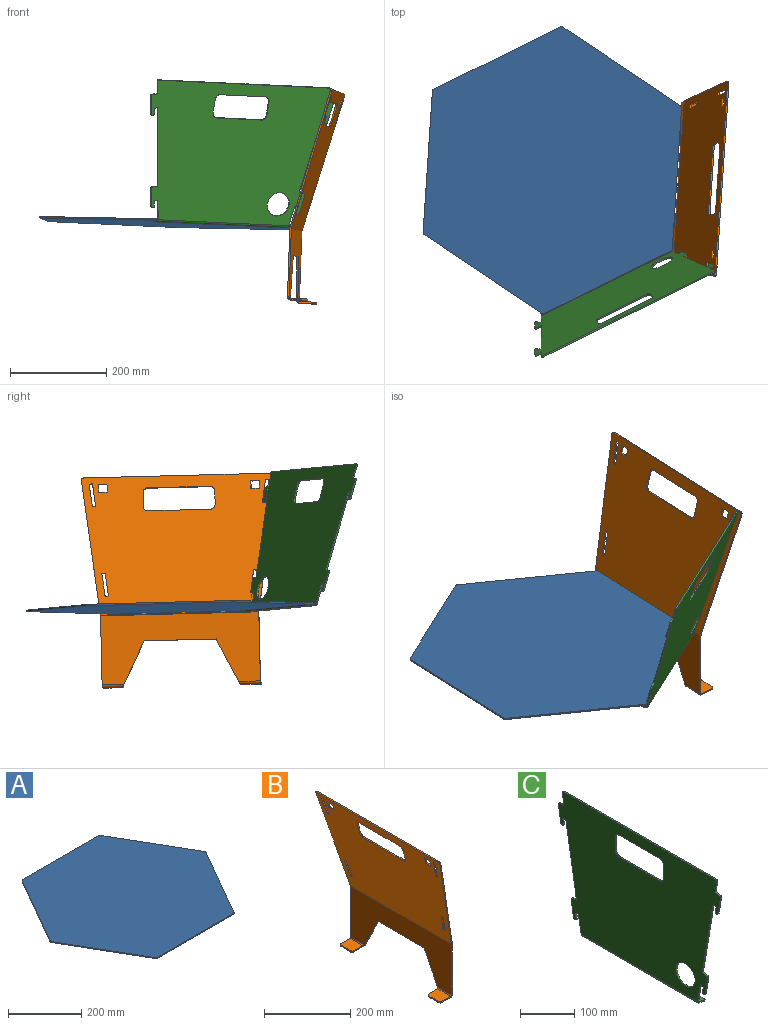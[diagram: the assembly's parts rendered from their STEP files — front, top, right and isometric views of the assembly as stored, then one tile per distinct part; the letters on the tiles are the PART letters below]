
ASSEMBLY  parts=3 mates=3
PART A: 14 faces, bbox 598.5x519.6x3 mm
  f0: plane 294.23x3mm, normal (0,-1,0), area 882.7mm2, adj f6,f7,f8,f13
  f1: plane 254.81x147.11mm, normal (0.87,-0.5,0), area 882.7mm2, adj f6,f7,f8,f9
  f2: plane 254.81x147.11mm, normal (0.87,0.5,0), area 882.7mm2, adj f6,f7,f9,f10
  f3: plane 294.23x3mm, normal (0,1,0), area 882.7mm2, adj f6,f7,f10,f11
  f4: plane 254.81x147.11mm, normal (-0.87,0.5,0), area 882.7mm2, adj f6,f7,f11,f12
  f5: plane 254.81x147.11mm, normal (-0.87,-0.5,0), area 882.7mm2, adj f6,f7,f12,f13
  f6: plane 598.45x519.62mm, normal (0,0,1), area 233818.8mm2, adj f0,f1,f2,f3,f4,f5,f8,f9
  f7: plane 598.45x519.62mm, normal (0,0,-1), area 233818.8mm2, adj f0,f1,f2,f3,f4,f5,f8,f9
  f8: cylinder r=5mm len=4.33mm, axis (0,0,-1), area 15.7mm2, adj f0,f1,f6,f7
  f9: cylinder r=5mm len=5mm, axis (0,0,-1), area 15.7mm2, adj f1,f2,f6,f7
  f10: cylinder r=5mm len=4.33mm, axis (0,0,-1), area 15.7mm2, adj f2,f3,f6,f7
  f11: cylinder r=5mm len=4.33mm, axis (0,0,-1), area 15.7mm2, adj f3,f4,f6,f7
  f12: cylinder r=5mm len=5mm, axis (0,0,-1), area 15.7mm2, adj f4,f5,f6,f7
  f13: cylinder r=5mm len=4.33mm, axis (0,0,-1), area 15.7mm2, adj f0,f5,f6,f7
PART B: 72 faces, bbox 80.7x407x439.8 mm
  f0: plane 150x3.18mm, normal (0,0,-1), area 476.3mm2, adj f1,f4,f5,f6
  f1: plane 89.53x44.76mm, normal (0,0.89,-0.45), area 317.8mm2, adj f0,f5,f6,f58
  f2: plane 143.8x3.18mm, normal (0,-1,0), area 456.6mm2, adj f5,f6,f46,f57
  f3: plane 143.8x3.18mm, normal (0,1,0), area 456.6mm2, adj f5,f6,f47,f69
  f4: plane 89.53x44.76mm, normal (0,-0.89,-0.45), area 317.8mm2, adj f0,f5,f6,f68
  f5: plane 330x143.8mm, normal (-1,0,0), area 30019.3mm2, adj f0,f1,f2,f3,f4,f49,f60,f71
  f6: plane 330x143.8mm, normal (1,0,0), area 30019.3mm2, adj f0,f1,f2,f3,f4,f48,f59,f70
  f7: plane 407.03x289.08mm, normal (0.97,0,0.26), area 101115mm2, adj f8,f10,f11,f12,f13,f14,f15,f16
  f8: plane 284.45x79.06mm, normal (0.03,-0.99,-0.13), area 940.2mm2, adj f7,f9,f45,f46
  f9: plane 407.03x289.08mm, normal (-0.97,0,-0.26), area 101115mm2, adj f8,f10,f11,f12,f13,f14,f15,f16
  f10: plane 284.45x79.06mm, normal (0.03,0.99,-0.13), area 940.2mm2, adj f7,f9,f44,f47
  f11: plane 130x3.07mm, normal (0.26,0,-0.97), area 412.7mm2, adj f7,f9,f12,f43
  f12: cylinder r=10mm len=10.48mm, axis (-0.97,0,-0.26), area 49.9mm2, adj f7,f9,f11,f13
  f13: plane 29.8x10.83mm, normal (0,1,0), area 95.2mm2, adj f7,f9,f12,f14
  f14: cylinder r=10mm len=10.48mm, axis (-0.97,0,-0.26), area 49.9mm2, adj f7,f9,f13,f15
  f15: plane 130x3.07mm, normal (-0.26,0,0.97), area 412.8mm2, adj f7,f9,f14,f16
  f16: cylinder r=10mm len=10.48mm, axis (-0.97,0,-0.26), area 49.9mm2, adj f7,f9,f15,f17
  f17: plane 29.8x10.83mm, normal (0,-1,0), area 95.3mm2, adj f7,f9,f16,f43
  f18: plane 48.71x15.9mm, normal (0.03,-0.99,-0.13), area 158.8mm2, adj f7,f9,f19,f42
  f19: plane 6.94x3.3mm, normal (0.26,0.13,-0.96), area 22.2mm2, adj f7,f9,f18,f20
  f20: plane 48.71x15.9mm, normal (-0.03,0.99,0.13), area 158.8mm2, adj f7,f9,f19,f42
  f21: plane 17.24x7.47mm, normal (0,-1,0), area 54mm2, adj f7,f9,f22,f41
  f22: plane 17x3.07mm, normal (0.26,0,-0.97), area 54mm2, adj f7,f9,f21,f23
  f23: plane 17.24x7.47mm, normal (0,1,0), area 54mm2, adj f7,f9,f22,f41
  f24: plane 48.71x15.9mm, normal (0.03,-0.99,-0.13), area 158.8mm2, adj f7,f9,f25,f40
  f25: plane 6.94x3.3mm, normal (0.26,0.13,-0.96), area 22.2mm2, adj f7,f9,f24,f26
  f26: plane 48.71x15.9mm, normal (-0.03,0.99,0.13), area 158.7mm2, adj f7,f9,f25,f40
  f27: plane 17.24x7.47mm, normal (0,-1,0), area 54mm2, adj f7,f9,f28,f39
  f28: plane 17x3.07mm, normal (0.26,0,-0.97), area 54mm2, adj f7,f9,f27,f29
  f29: plane 17.24x7.47mm, normal (0,1,0), area 54mm2, adj f7,f9,f28,f39
  f30: plane 6.94x3.3mm, normal (0.26,-0.13,-0.96), area 22.2mm2, adj f7,f9,f31,f38
  f31: plane 48.71x15.9mm, normal (0.03,0.99,-0.13), area 158.8mm2, adj f7,f9,f30,f32
  f32: plane 6.94x3.3mm, normal (-0.26,0.13,0.96), area 22.2mm2, adj f7,f9,f31,f38
  f33: plane 6.94x3.3mm, normal (0.26,-0.13,-0.96), area 22.2mm2, adj f7,f9,f34,f37
  f34: plane 48.71x15.9mm, normal (0.03,0.99,-0.13), area 158.7mm2, adj f7,f9,f33,f35
  f35: plane 6.94x3.3mm, normal (-0.26,0.13,0.96), area 22.2mm2, adj f7,f9,f34,f37
  f36: plane 397.03x3.07mm, normal (-0.26,0,0.97), area 1260.6mm2, adj f7,f9,f44,f45
  f37: plane 48.71x15.9mm, normal (-0.03,-0.99,0.13), area 158.7mm2, adj f7,f9,f33,f35
  f38: plane 48.71x15.9mm, normal (-0.03,-0.99,0.13), area 158.7mm2, adj f7,f9,f30,f32
  f39: plane 17x3.07mm, normal (-0.26,0,0.97), area 54mm2, adj f7,f9,f27,f29
  f40: plane 6.94x3.3mm, normal (-0.26,-0.13,0.96), area 22.2mm2, adj f7,f9,f24,f26
  f41: plane 17x3.07mm, normal (-0.26,0,0.97), area 54mm2, adj f7,f9,f21,f23
  f42: plane 6.94x3.3mm, normal (-0.26,-0.13,0.96), area 22.2mm2, adj f7,f9,f18,f20
  f43: cylinder r=10mm len=10.48mm, axis (-0.97,0,-0.26), area 49.9mm2, adj f7,f9,f11,f17
  f44: cylinder r=5mm len=6.28mm, axis (0.97,0,0.26), area 27mm2, adj f7,f9,f10,f36
  f45: cylinder r=5mm len=6.28mm, axis (0.97,0,0.26), area 27mm2, adj f7,f8,f9,f36
  f46: bspline ~3.25x1.42mm, area 3.2mm2, adj f2,f8,f48,f49
  f47: bspline ~3.25x1.42mm, area 3.2mm2, adj f3,f10,f48,f49
  f48: cylinder r=5.47mm len=330.16mm, axis (0,-1,0), area 473.1mm2, adj f6,f7,f46,f47
  f49: cylinder r=2.3mm len=330.16mm, axis (0,-1,0), area 198.8mm2, adj f5,f9,f46,f47
  f50: plane 32.5x3.18mm, normal (-1,0,0), area 103.2mm2, adj f53,f54,f55,f56
  f51: plane 29.53x3.18mm, normal (0,-1,0), area 93.7mm2, adj f53,f54,f55,f57
  f52: plane 29.53x3.18mm, normal (0,1,0), area 93.7mm2, adj f53,f54,f56,f58
  f53: plane 42.5x34.53mm, normal (0,0,1), area 1456.6mm2, adj f50,f51,f52,f55,f56,f60
  f54: plane 42.5x34.53mm, normal (0,0,-1), area 1456.6mm2, adj f50,f51,f52,f55,f56,f59
  f55: cylinder r=5mm len=5mm, axis (0,0,1), area 24.9mm2, adj f50,f51,f53,f54
  f56: cylinder r=5mm len=5mm, axis (0,0,1), area 24.9mm2, adj f50,f52,f53,f54
  f57: plane 5.48x5.48mm, normal (0,-1,0), area 19.4mm2, adj f2,f51,f59,f60
  f58: bspline ~5.48x5.48mm, area 21.7mm2, adj f1,f52,f59,f60
  f59: cylinder r=5.47mm len=45.24mm, axis (0,-1,0), area 374mm2, adj f6,f54,f57,f58
  f60: cylinder r=2.3mm len=45.24mm, axis (0,-1,0), area 157.1mm2, adj f5,f53,f57,f58
  f61: plane 29.53x3.18mm, normal (0,1,0), area 93.7mm2, adj f64,f65,f67,f69
  f62: plane 32.5x3.18mm, normal (-1,0,0), area 103.2mm2, adj f64,f65,f66,f67
  f63: plane 29.53x3.18mm, normal (0,-1,0), area 93.7mm2, adj f64,f65,f66,f68
  f64: plane 42.5x34.53mm, normal (0,0,1), area 1456.6mm2, adj f61,f62,f63,f66,f67,f71
  f65: plane 42.5x34.53mm, normal (0,0,-1), area 1456.6mm2, adj f61,f62,f63,f66,f67,f70
  f66: cylinder r=5mm len=5mm, axis (0,0,1), area 24.9mm2, adj f62,f63,f64,f65
  f67: cylinder r=5mm len=5mm, axis (0,0,1), area 24.9mm2, adj f61,f62,f64,f65
  f68: bspline ~5.48x5.48mm, area 21.7mm2, adj f4,f63,f70,f71
  f69: plane 5.48x5.48mm, normal (0,1,0), area 19.4mm2, adj f3,f61,f70,f71
  f70: cylinder r=5.47mm len=45.24mm, axis (0,-1,0), area 374.1mm2, adj f6,f65,f68,f69
  f71: cylinder r=2.3mm len=45.24mm, axis (0,-1,0), area 157.1mm2, adj f5,f64,f68,f69
PART C: 63 faces, bbox 22.5x422.1x308.2 mm
  f0: plane 30x3.18mm, normal (0,-1,0), area 95.2mm2, adj f1,f35,f36,f37
  f1: cylinder r=10mm len=10mm, axis (-1,0,0), area 49.9mm2, adj f0,f2,f36,f37
  f2: plane 105x3.18mm, normal (0,0,-1), area 333.4mm2, adj f1,f3,f36,f37
  f3: cylinder r=10mm len=10mm, axis (-1,0,0), area 49.9mm2, adj f2,f4,f36,f37
  f4: plane 30x3.18mm, normal (0,1,0), area 95.2mm2, adj f3,f5,f36,f37
  f5: cylinder r=10mm len=10mm, axis (-1,0,0), area 49.9mm2, adj f4,f6,f36,f37
  f6: plane 105x3.18mm, normal (0,0,1), area 333.4mm2, adj f5,f35,f36,f37
  f7: plane 11.84x3.18mm, normal (0,0.17,0.99), area 38.1mm2, adj f34,f36,f37,f50
  f8: plane 38.46x6.45mm, normal (0,0.99,-0.17), area 123.8mm2, adj f36,f37,f43,f50
  f9: plane 3.18x0.99mm, normal (0,-0.17,-0.99), area 3.2mm2, adj f36,f37,f40,f43
  f10: plane 11.84x3.18mm, normal (0,-0.99,0.17), area 38.1mm2, adj f11,f36,f37,f40
  f11: plane 7.89x3.18mm, normal (0,-0.17,-0.99), area 25.4mm2, adj f10,f12,f36,f37
  f12: plane 167.66x28.1mm, normal (0,0.99,-0.17), area 539.8mm2, adj f11,f13,f36,f37
  f13: plane 11.84x3.18mm, normal (0,0.17,0.99), area 38.1mm2, adj f12,f36,f37,f51
  f14: plane 38.46x6.45mm, normal (0,0.99,-0.17), area 123.8mm2, adj f36,f37,f49,f51
  f15: plane 3.18x0.99mm, normal (0,-0.17,-0.99), area 3.2mm2, adj f36,f37,f48,f49
  f16: plane 11.84x3.18mm, normal (0,-0.99,0.17), area 38.1mm2, adj f17,f36,f37,f48
  f17: plane 7.89x3.18mm, normal (0,-0.17,-0.99), area 25.4mm2, adj f16,f18,f36,f37
  f18: plane 41.88x7.02mm, normal (0,0.99,-0.17), area 134.8mm2, adj f17,f36,f37,f60
  f19: plane 41.88x7.02mm, normal (0,-0.99,-0.17), area 134.8mm2, adj f20,f36,f37,f59
  f20: plane 7.89x3.18mm, normal (0,0.17,-0.99), area 25.4mm2, adj f19,f21,f36,f37
  f21: plane 11.84x3.18mm, normal (0,0.99,0.17), area 38.1mm2, adj f20,f36,f37,f38
  f22: plane 3.18x0.99mm, normal (0,0.17,-0.99), area 3.2mm2, adj f36,f37,f38,f41
  f23: plane 38.46x6.45mm, normal (0,-0.99,-0.17), area 123.8mm2, adj f36,f37,f41,f46
  f24: plane 11.84x3.18mm, normal (0,-0.17,0.99), area 38.1mm2, adj f25,f36,f37,f46
  f25: plane 167.66x28.1mm, normal (0,-0.99,-0.17), area 539.8mm2, adj f24,f26,f36,f37
  f26: plane 7.89x3.18mm, normal (0,0.17,-0.99), area 25.4mm2, adj f25,f27,f36,f37
  f27: plane 11.84x3.18mm, normal (0,0.99,0.17), area 38.1mm2, adj f26,f36,f37,f42
  f28: plane 3.18x0.99mm, normal (0,0.17,-0.99), area 3.2mm2, adj f36,f37,f39,f42
  f29: plane 38.46x6.45mm, normal (0,-0.99,-0.17), area 123.8mm2, adj f36,f37,f39,f47
  f30: plane 11.84x3.18mm, normal (0,-0.17,0.99), area 38.1mm2, adj f31,f36,f37,f47
  f31: plane 26.02x4.36mm, normal (0,-0.99,-0.17), area 83.8mm2, adj f30,f36,f37,f44
  f32: plane 396.23x3.18mm, normal (0,0,1), area 1258mm2, adj f36,f37,f44,f45
  f33: cylinder r=25mm len=50mm, axis (-1,0,0), area 498.7mm2, adj f36,f37
  f34: plane 26.02x4.36mm, normal (0,0.99,-0.17), area 83.8mm2, adj f7,f36,f37,f45
  f35: cylinder r=10mm len=10mm, axis (-1,0,0), area 49.9mm2, adj f0,f6,f36,f37
  f36: plane 422.11x298.24mm, normal (-1,0,0), area 99441.4mm2, adj f0,f1,f2,f3,f4,f5,f6,f7
  f37: plane 422.11x298.24mm, normal (1,0,0), area 99441.4mm2, adj f0,f1,f2,f3,f4,f5,f6,f7
  f38: cylinder r=3mm len=3.45mm, axis (-1,0,0), area 15mm2, adj f21,f22,f36,f37
  f39: cylinder r=3mm len=3.45mm, axis (-1,0,0), area 15mm2, adj f28,f29,f36,f37
  f40: cylinder r=3mm len=3.45mm, axis (-1,0,0), area 15mm2, adj f9,f10,f36,f37
  f41: cylinder r=3mm len=3.45mm, axis (-1,0,0), area 15mm2, adj f22,f23,f36,f37
  f42: cylinder r=3mm len=3.45mm, axis (-1,0,0), area 15mm2, adj f27,f28,f36,f37
  f43: cylinder r=3mm len=3.45mm, axis (-1,0,0), area 15mm2, adj f8,f9,f36,f37
  f44: cylinder r=3mm len=3.5mm, axis (1,0,0), area 16.5mm2, adj f31,f32,f36,f37
  f45: cylinder r=3mm len=3.5mm, axis (1,0,0), area 16.5mm2, adj f32,f34,f36,f37
  f46: cylinder r=3mm len=3.45mm, axis (-1,0,0), area 15mm2, adj f23,f24,f36,f37
  f47: cylinder r=3mm len=3.45mm, axis (-1,0,0), area 15mm2, adj f29,f30,f36,f37
  f48: cylinder r=3mm len=3.45mm, axis (-1,0,0), area 15mm2, adj f15,f16,f36,f37
  f49: cylinder r=3mm len=3.45mm, axis (-1,0,0), area 15mm2, adj f14,f15,f36,f37
  f50: cylinder r=3mm len=3.45mm, axis (-1,0,0), area 15mm2, adj f7,f8,f36,f37
  f51: cylinder r=3mm len=3.45mm, axis (-1,0,0), area 15mm2, adj f13,f14,f36,f37
  f52: plane 294.25x3.07mm, normal (0.97,0,-0.26), area 934.2mm2, adj f55,f56,f57,f58
  f53: plane 15.66x7.04mm, normal (0.04,-1,-0.01), area 48.8mm2, adj f55,f56,f57,f59
  f54: plane 15.66x7.04mm, normal (0.04,1,-0.01), area 48.8mm2, adj f55,f56,f58,f60
  f55: plane 301.58x17.61mm, normal (-0.26,0,-0.97), area 5481.4mm2, adj f52,f53,f54,f57,f58,f61
  f56: plane 301.58x17.61mm, normal (0.26,0,0.97), area 5481.4mm2, adj f52,f53,f54,f57,f58,f62
  f57: cylinder r=3mm len=3.81mm, axis (-0.26,0,-0.97), area 14.5mm2, adj f52,f53,f55,f56
  f58: cylinder r=3mm len=3.81mm, axis (-0.26,0,-0.97), area 14.5mm2, adj f52,f54,f55,f56
  f59: bspline ~5.29x4.88mm, area 16.4mm2, adj f19,f53,f61,f62
  f60: bspline ~5.29x4.88mm, area 16.5mm2, adj f18,f54,f61,f62
  f61: cylinder r=5.47mm len=303.35mm, axis (0,-1,0), area 2167.7mm2, adj f36,f55,f59,f60
  f62: cylinder r=2.3mm len=303.35mm, axis (0,-1,0), area 910.6mm2, adj f37,f56,f59,f60
PLACE A rot(axis=(0.01,0.03,1),86.2deg) t=(-17.1,6.76,-10.38)mm fixed
PLACE B rot(axis=(0.02,0.01,1),176.2deg) t=(272.98,-276.72,128.28)mm
PLACE C rot(axis=(0.14,-0.06,0.99),116.5deg) t=(-117.18,-376.36,147.02)mm
MATE planar C.f56 <-> A.f7  axis (0.03,0.02,1) through (91.17,-219.37,-8.92)mm
MATE parallel A.f0 <-> B.f6  axis (1,-0.07,-0.03) through (242.04,-10.54,-17.53)mm
MATE parallel B.f54 <-> A.f7  axis (-0.03,-0.02,-1) through (273.45,125.26,-176.2)mm
